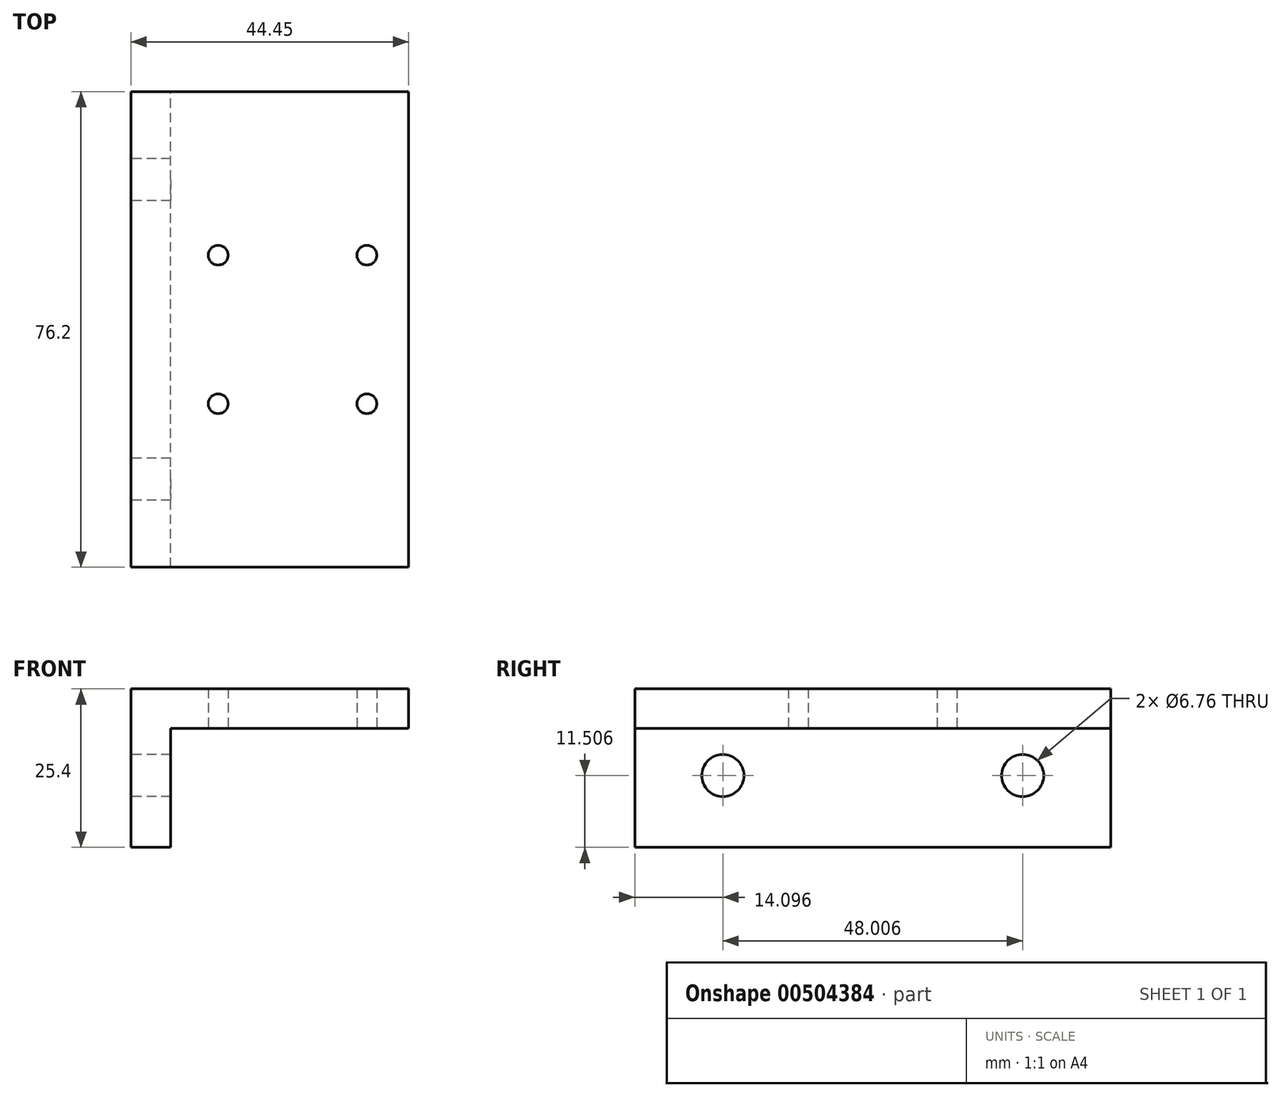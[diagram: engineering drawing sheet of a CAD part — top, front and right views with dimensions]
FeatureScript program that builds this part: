
annotation { "Feature Type Name" : "Feature", "Feature Type Description" : "" }
export const myFeature = defineFeature(function(context is Context, id is Id, definition is map)
    precondition{}
    {
        {
            var Q0;
            Q0=qCreatedBy(makeId("Top.planeOp"),FACE);
            var sketch = newSketch(context, id + "F0", { "sketchPlane" : qUnion([Q0])});
            skLineSegment(sketch, "E0.bottom", {"start": v(-97.54, 64.66) * mm, "end": v(-53.1, 64.66) * mm});
            skLineSegment(sketch, "E0.top", {"start": v(-97.54, -11.54) * mm, "end": v(-53.1, -11.54) * mm});
            skLineSegment(sketch, "E0.left", {"start": v(-97.54, 64.66) * mm, "end": v(-97.54, -11.54) * mm});
            skLineSegment(sketch, "E0.right", {"start": v(-53.1, 64.66) * mm, "end": v(-53.1, -11.54) * mm});
            skSolve(sketch);
        }
        {
            var Q0;
            Q0=makeQuery(id+"F0.imprint","IMPRINT",FACE,{"disambiguationData":[TD([[makeQuery(id+"F0.imprint","IMPRINT",EDGE,{"derivedFrom":sQuery(id+"F0.wireOp",EDGE,"E0.bottom")}),-1.0]])]});
            extrude(context, id + "F1", {"entities" : qUnion([Q0]), "depth" : 6.35 * mm});
        }
        {
            var Q0;
            Q0=makeQuery(id+"F1.opExtrude","CAP_FACE",FACE,{"disambiguationData":[OSD([sQuery(id+"F0.wireOp",EDGE,"E0.bottom"),sQuery(id+"F0.wireOp",EDGE,"E0.top"),sQuery(id+"F0.wireOp",EDGE,"E0.left"),sQuery(id+"F0.wireOp",EDGE,"E0.right")])],"isStart":true});
            var sketch = newSketch(context, id + "F2", { "sketchPlane" : qUnion([Q0])});
            skLineSegment(sketch, "E1.bottom", {"start": v(-97.54, 11.54) * mm, "end": v(-91.2, 11.54) * mm});
            skLineSegment(sketch, "E1.top", {"start": v(-97.54, -64.66) * mm, "end": v(-91.2, -64.66) * mm});
            skLineSegment(sketch, "E1.left", {"start": v(-97.54, 11.54) * mm, "end": v(-97.54, -64.66) * mm});
            skLineSegment(sketch, "E1.right", {"start": v(-91.2, 11.54) * mm, "end": v(-91.2, -64.66) * mm});
            skSolve(sketch);
        }
        {
            var Q0;
            Q0 = qSketchRegion(id + "F2", true);
            extrude(context, id + "F3", {"entities" : qUnion([Q0]), "operationType" : NewBodyOperationType.ADD, "depth" : 19.05 * mm});
        }
        {
            var Q0;
            Q0=makeQuery(id+"F3.boolean.opBoolean","MERGE",FACE,{"derivedFrom":[makeQuery(id+"F1.opExtrude","SWEPT_FACE",FACE,{"disambiguationData":[OSD([sQuery(id+"F0.wireOp",EDGE,"E0.left")])]}),makeQuery(id+"F3.opExtrude","SWEPT_FACE",FACE,{"disambiguationData":[OSD([sQuery(id+"F2.wireOp",EDGE,"E1.left")])]})]});
            var sketch = newSketch(context, id + "F4", { "sketchPlane" : qUnion([Q0])});
            skCircle(sketch, "E2", {"center": v(-50.56, -7.54) * mm, "radius": 3.38 * mm});
            skCircle(sketch, "E3", {"center": v(-2.56, -7.54) * mm, "radius": 3.38 * mm});
            skSolve(sketch);
        }
        {
            var Q0;
            Q0=makeQuery(id+"F4.imprint","IMPRINT",FACE,{"disambiguationData":[TD([[makeQuery(id+"F4.imprint","IMPRINT",EDGE,{"derivedFrom":sQuery(id+"F4.wireOp",EDGE,"E3")}),1.0]])]});
            var Q1;
            Q1=makeQuery(id+"F4.imprint","IMPRINT",FACE,{"disambiguationData":[TD([[makeQuery(id+"F4.imprint","IMPRINT",EDGE,{"derivedFrom":sQuery(id+"F4.wireOp",EDGE,"E2")}),1.0]])]});
            var Q2;
            Q2=sQuery(id+"F4.wireOp",EDGE,"E3");
            var Q3;
            Q3=sQuery(id+"F4.wireOp",EDGE,"E2");
            extrude(context, id + "F5", {"entities" : qUnion([Q0, Q1]), "operationType" : NewBodyOperationType.REMOVE, "surfaceEntities" : qUnion([Q2, Q3]), "oppositeDirection" : true, "depth" : 12.7 * mm});
        }
        {
            var Q0;
            Q0=makeQuery(id+"F1.opExtrude","CAP_FACE",FACE,{"disambiguationData":[OSD([sQuery(id+"F0.wireOp",EDGE,"E0.bottom"),sQuery(id+"F0.wireOp",EDGE,"E0.top"),sQuery(id+"F0.wireOp",EDGE,"E0.left"),sQuery(id+"F0.wireOp",EDGE,"E0.right")])],"isStart":true});
            var sketch = newSketch(context, id + "F6", { "sketchPlane" : qUnion([Q0])});
            skCircle(sketch, "E4", {"center": v(-83.57, -14.65) * mm, "radius": 1.59 * mm});
            skCircle(sketch, "E5", {"center": v(-59.76, -14.65) * mm, "radius": 1.59 * mm});
            skCircle(sketch, "E6", {"center": v(-83.57, -38.47) * mm, "radius": 1.59 * mm});
            skCircle(sketch, "E7", {"center": v(-59.76, -38.47) * mm, "radius": 1.59 * mm});
            skLineSegment(sketch, "E8", {"start": v(-83.57, -14.65) * mm, "end": v(-83.57, -38.47) * mm});
            skLineSegment(sketch, "E9", {"start": v(-59.76, -38.47) * mm, "end": v(-83.57, -38.47) * mm});
            skLineSegment(sketch, "E10", {"start": v(-59.76, -38.47) * mm, "end": v(-59.76, -14.65) * mm});
            skLineSegment(sketch, "E11", {"start": v(-83.57, -14.65) * mm, "end": v(-59.76, -14.65) * mm});
            skSolve(sketch);
        }
        {
            var Q0;
            {var subQ0=sQuery(id+"F6.wireOp",EDGE,"E8");var subQ1=sQuery(id+"F6.wireOp",EDGE,"E4");var subQ2=makeQuery(id+"F6.imprint","INTERSECT",VERTEX,{"derivedFrom":[subQ1,subQ0]});Q0=makeQuery(id+"F6.imprint","IMPRINT",FACE,{"disambiguationData":[TD([[makeQuery(id+"F6.imprint","IMPRINT",EDGE,{"disambiguationData":[TD([[subQ2,1.0]])],"derivedFrom":subQ1}),1.0]])]});}
            var Q1;
            {var subQ0=sQuery(id+"F6.wireOp",EDGE,"E8");var subQ1=sQuery(id+"F6.wireOp",EDGE,"E4");var subQ2=makeQuery(id+"F6.imprint","INTERSECT",VERTEX,{"derivedFrom":[subQ1,subQ0]});Q1=makeQuery(id+"F6.imprint","IMPRINT",FACE,{"disambiguationData":[TD([[makeQuery(id+"F6.imprint","IMPRINT",EDGE,{"disambiguationData":[TD([[subQ2,-1.0]])],"derivedFrom":subQ1}),1.0]])]});}
            var Q2;
            {var subQ0=sQuery(id+"F6.wireOp",EDGE,"E10");var subQ1=sQuery(id+"F6.wireOp",EDGE,"E5");var subQ2=makeQuery(id+"F6.imprint","INTERSECT",VERTEX,{"derivedFrom":[subQ1,subQ0]});Q2=makeQuery(id+"F6.imprint","IMPRINT",FACE,{"disambiguationData":[TD([[makeQuery(id+"F6.imprint","IMPRINT",EDGE,{"disambiguationData":[TD([[subQ2,-1.0]])],"derivedFrom":subQ1}),1.0]])]});}
            var Q3;
            {var subQ0=sQuery(id+"F6.wireOp",EDGE,"E10");var subQ1=sQuery(id+"F6.wireOp",EDGE,"E5");var subQ2=makeQuery(id+"F6.imprint","INTERSECT",VERTEX,{"derivedFrom":[subQ1,subQ0]});Q3=makeQuery(id+"F6.imprint","IMPRINT",FACE,{"disambiguationData":[TD([[makeQuery(id+"F6.imprint","IMPRINT",EDGE,{"disambiguationData":[TD([[subQ2,1.0]])],"derivedFrom":subQ1}),1.0]])]});}
            var Q4;
            {var subQ0=sQuery(id+"F6.wireOp",EDGE,"E8");var subQ1=sQuery(id+"F6.wireOp",EDGE,"E6");var subQ2=makeQuery(id+"F6.imprint","INTERSECT",VERTEX,{"derivedFrom":[subQ1,subQ0]});Q4=makeQuery(id+"F6.imprint","IMPRINT",FACE,{"disambiguationData":[TD([[makeQuery(id+"F6.imprint","IMPRINT",EDGE,{"disambiguationData":[TD([[subQ2,1.0]])],"derivedFrom":subQ1}),1.0]])]});}
            var Q5;
            {var subQ0=sQuery(id+"F6.wireOp",EDGE,"E8");var subQ1=sQuery(id+"F6.wireOp",EDGE,"E6");var subQ2=makeQuery(id+"F6.imprint","INTERSECT",VERTEX,{"derivedFrom":[subQ1,subQ0]});Q5=makeQuery(id+"F6.imprint","IMPRINT",FACE,{"disambiguationData":[TD([[makeQuery(id+"F6.imprint","IMPRINT",EDGE,{"disambiguationData":[TD([[subQ2,-1.0]])],"derivedFrom":subQ1}),1.0]])]});}
            var Q6;
            {var subQ0=sQuery(id+"F6.wireOp",EDGE,"E9");var subQ1=sQuery(id+"F6.wireOp",EDGE,"E7");var subQ2=makeQuery(id+"F6.imprint","INTERSECT",VERTEX,{"derivedFrom":[subQ1,subQ0]});Q6=makeQuery(id+"F6.imprint","IMPRINT",FACE,{"disambiguationData":[TD([[makeQuery(id+"F6.imprint","IMPRINT",EDGE,{"disambiguationData":[TD([[subQ2,1.0]])],"derivedFrom":subQ1}),1.0]])]});}
            var Q7;
            {var subQ0=sQuery(id+"F6.wireOp",EDGE,"E9");var subQ1=sQuery(id+"F6.wireOp",EDGE,"E7");var subQ2=makeQuery(id+"F6.imprint","INTERSECT",VERTEX,{"derivedFrom":[subQ1,subQ0]});Q7=makeQuery(id+"F6.imprint","IMPRINT",FACE,{"disambiguationData":[TD([[makeQuery(id+"F6.imprint","IMPRINT",EDGE,{"disambiguationData":[TD([[subQ2,-1.0]])],"derivedFrom":subQ1}),1.0]])]});}
            extrude(context, id + "F7", {"entities" : qUnion([Q0, Q1, Q2, Q3, Q4, Q5, Q6, Q7]), "operationType" : NewBodyOperationType.REMOVE, "oppositeDirection" : true, "depth" : 25.4 * mm});
        }
    });
